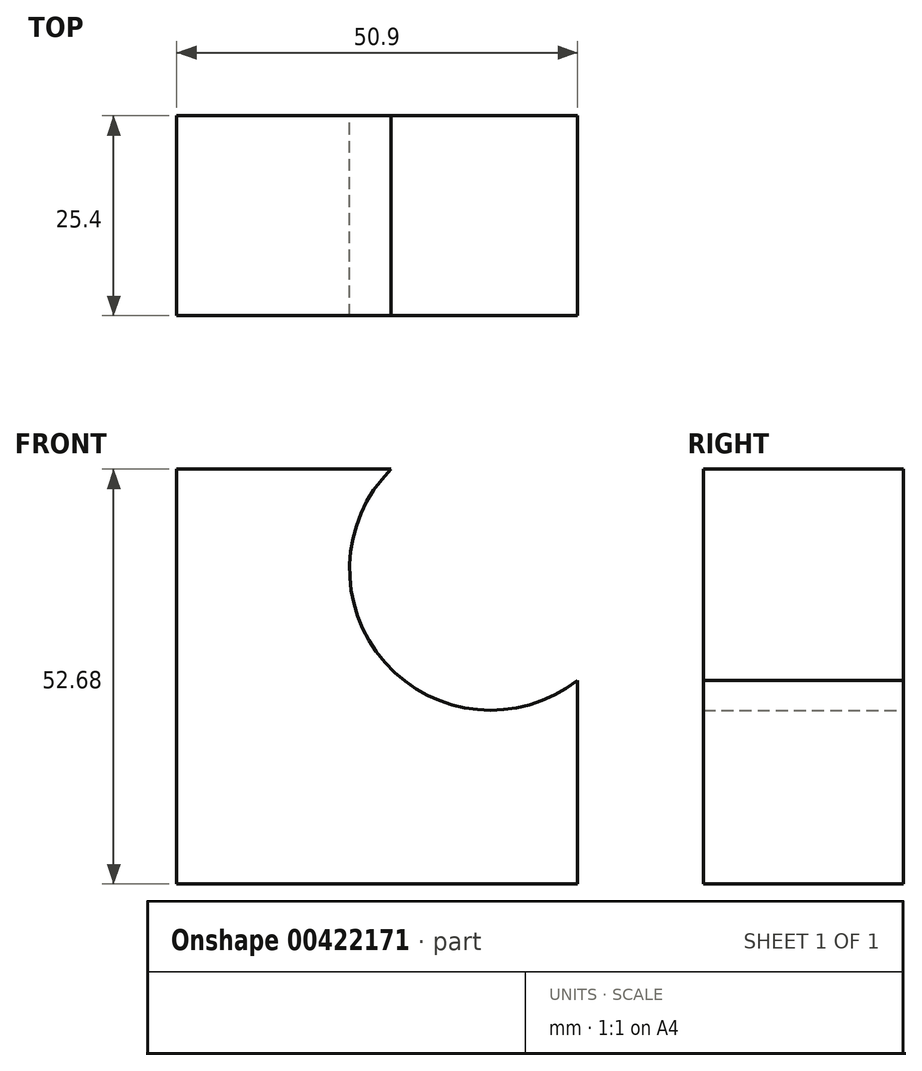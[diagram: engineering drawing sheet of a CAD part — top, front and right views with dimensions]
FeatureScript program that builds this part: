
annotation { "Feature Type Name" : "Feature", "Feature Type Description" : "" }
export const myFeature = defineFeature(function(context is Context, id is Id, definition is map)
    precondition{}
    {
        {
            var Q0;
            Q0=qCreatedBy(makeId("Front.planeOp"),FACE);
            var sketch = newSketch(context, id + "F0", { "sketchPlane" : qUnion([Q0])});
            skLineSegment(sketch, "E0", {"start": v(-63.63, 50.41) * mm, "end": v(-36.4, 50.41) * mm});
            skLineSegment(sketch, "E1", {"start": v(-63.63, 50.41) * mm, "end": v(-63.63, -2.27) * mm});
            skLineSegment(sketch, "E2", {"start": v(-63.63, -2.27) * mm, "end": v(-12.73, -2.27) * mm});
            skLineSegment(sketch, "E3", {"start": v(-12.73, -2.27) * mm, "end": v(-12.73, 23.58) * mm});
            skArc(sketch, "E4", {"start": v(-36.4, 50.41) * mm, "mid": v(-37.2, 25.85) * mm, "end": v(-12.73, 23.58) * mm});
            skSolve(sketch);
        }
        {
            var Q0;
            Q0=makeQuery(id+"F0.imprint","IMPRINT",FACE,{"disambiguationData":[TD([[makeQuery(id+"F0.imprint","IMPRINT",EDGE,{"derivedFrom":sQuery(id+"F0.wireOp",EDGE,"E0")}),-1.0]])]});
            extrude(context, id + "F1", {"entities" : qUnion([Q0]), "depth" : 25.4 * mm});
        }
    });
